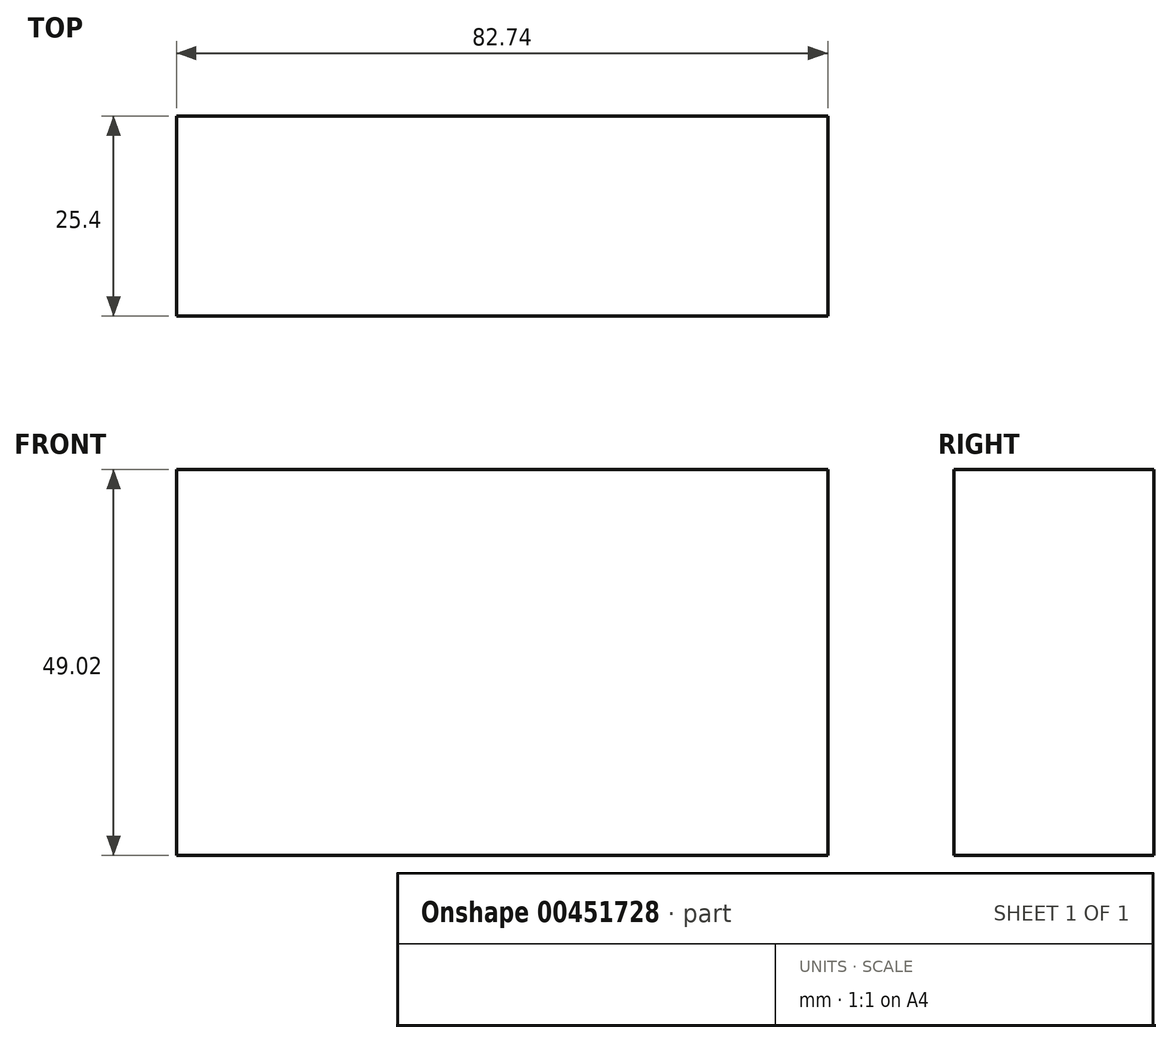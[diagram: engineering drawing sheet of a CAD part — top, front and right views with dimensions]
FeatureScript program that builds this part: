
annotation { "Feature Type Name" : "Feature", "Feature Type Description" : "" }
export const myFeature = defineFeature(function(context is Context, id is Id, definition is map)
    precondition{}
    {
        {
            var Q0;
            Q0=qCreatedBy(makeId("Front.planeOp"),FACE);
            var sketch = newSketch(context, id + "F0", { "sketchPlane" : qUnion([Q0])});
            skLineSegment(sketch, "E0.bottom", {"start": v(41.37, 31.5) * mm, "end": v(-41.37, 31.5) * mm});
            skLineSegment(sketch, "E0.top", {"start": v(41.37, -17.51) * mm, "end": v(-41.37, -17.51) * mm});
            skLineSegment(sketch, "E0.left", {"start": v(41.37, 31.5) * mm, "end": v(41.37, -17.51) * mm});
            skLineSegment(sketch, "E0.right", {"start": v(-41.37, 31.5) * mm, "end": v(-41.37, -17.51) * mm});
            skPoint(sketch, "E0.middle", {"position": v(0, 7) * mm});
            skSolve(sketch);
        }
        {
            var Q0;
            Q0=makeQuery(id+"F0.imprint","IMPRINT",FACE,{"disambiguationData":[TD([[makeQuery(id+"F0.imprint","IMPRINT",EDGE,{"derivedFrom":sQuery(id+"F0.wireOp",EDGE,"E0.bottom")}),1.0]])]});
            extrude(context, id + "F1", {"entities" : qUnion([Q0]), "depth" : 25.4 * mm});
        }
    });
